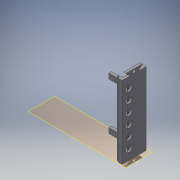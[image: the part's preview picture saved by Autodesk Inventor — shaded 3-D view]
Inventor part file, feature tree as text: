
AUTODESK INVENTOR PART (.ipt)
format: ipt  version: 2016 SP2 (Build 200236200, 236)  size: 286,720 bytes
history: native  units: mm
features: reference x14, extrude x8, sketch x8, chamfer x2, plane x1
ambient origin geometry x8: Origin, YZ Plane, XZ Plane, XY Plane, X Axis, Y Axis, Z Axis, Center Point
bodies: Volumenkörper1 (feature_tree)
feature tree (33):
  plane  "Arbeitsebene1"
  extrude  "Extrusion1"  Depth=0.6mm
  extrude  "Extrusion2"  Depth=15.0mm
  extrude  "Extrusion3"  Depth=4.5mm
  extrude  "Extrusion4"  TaperAngle=45.0deg  [1 undecoded]
  chamfer  "Fase1"  Distance=0.8mm
  extrude  "Extrusion5"  Depth=1.0mm
  extrude  "Extrusion6"  Depth=1.0mm
  chamfer  "Fase2"  Distance=0.8mm
  extrude  "Extrusion7"  Depth=1.0mm
  extrude  "Extrusion8"  Depth=2.0mm
  sketch  "Skizze1"  dims[d0=0.6mm d2=6.1mm]
  reference  "Referenz1"
  reference  "Referenz2"
  reference  "Referenz3"
  reference  "Referenz4"
  reference  "Referenz5"
  reference  "Referenz6"
  reference  "Referenz7"
  reference  "Referenz8"
  reference  "Referenz9"
  reference  "Referenz10"
  reference  "Referenz11"
  sketch  "Skizze2"  dims[d4=12.0mm d5=15.0mm]
  reference  "Referenz12"
  sketch  "Skizze3"  dims[d6=1.6mm d7=4.5mm]
  sketch  "Skizze4"  dims[d8=18.0mm d9=45.0deg]
  reference  "Referenz13"
  reference  "Referenz14"
  sketch  "Skizze5"  dims[d10=1.026067mm]
  sketch  "Skizze7"  dims[d11=6.0mm]
  sketch  "Skizze8"  dims[d12=1.0mm]
  sketch  "Skizze9"  dims[d13=0.8mm d14=0.8mm d15=1.0mm d16=1.0mm d17=0.8mm d18=1.0mm d19=2.0mm d20=138.8mm d21=0.0mm d22=4.4mm d23=0.0mm d24=6.0mm d25=6.0mm d26=3.5mm d27=0.0mm d28=32.65mm d29=0.0mm d30=2.5mm d31=2.0mm d32=45.0deg d33=3.5mm d34=3.5mm d35=5.0mm d36=5.0mm d37=5.0mm d38=5.0mm d39=36.75mm d40=0.0mm d41=5.8mm d43=5.8mm d44=2.5mm d45=0.0mm d46=2.0mm d47=2.0mm d48=45.0deg d49=15.0mm d50=19.4mm d51=60.0mm d53=20.0mm d54=10.0mm d56=10.0mm d58=19.4mm d59=3.9mm d60=0.0mm d61=12.0mm d62=12.0mm d63=12.0mm d64=12.0mm d65=12.0mm d66=12.0mm d67=3.9mm d68=0.0mm d69=3.9mm]
note: 1 required parameter value undecoded (feature->parameter linkage not recoverable at this tier; creation-order binding heuristic only, values carry confidence <= 0.55)
